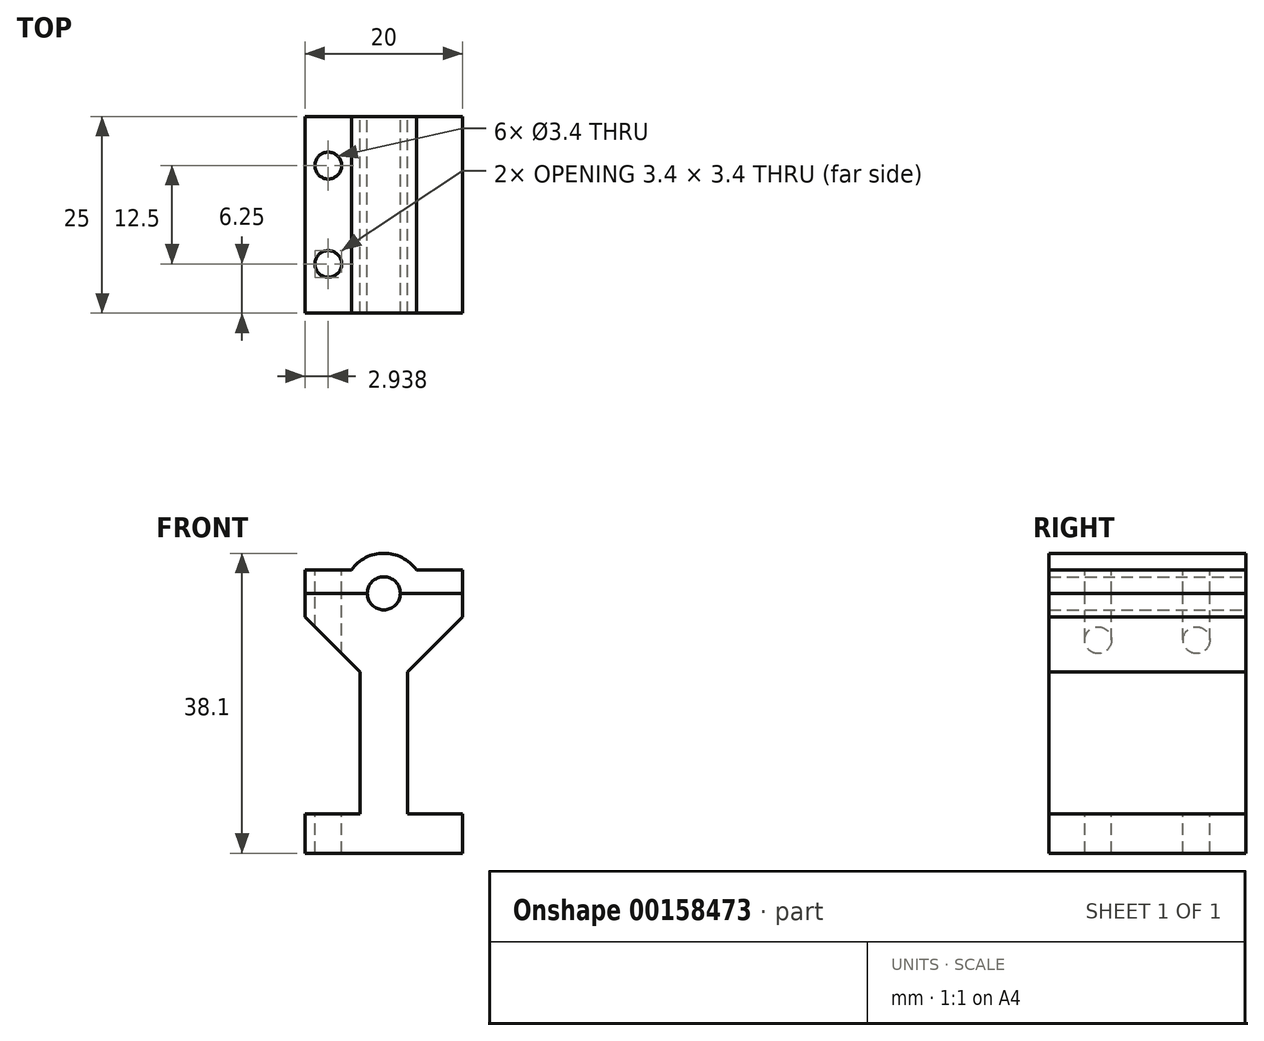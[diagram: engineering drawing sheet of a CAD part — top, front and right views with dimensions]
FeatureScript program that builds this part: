
annotation { "Feature Type Name" : "Feature", "Feature Type Description" : "" }
export const myFeature = defineFeature(function(context is Context, id is Id, definition is map)
    precondition{}
    {
        {
            var Q0;
            Q0=qCreatedBy(makeId("Front.planeOp"),FACE);
            var sketch = newSketch(context, id + "F0", { "sketchPlane" : qUnion([Q0])});
            skLineSegment(sketch, "E0", {"start": v(0, 0) * mm, "end": v(0, 53.37) * mm, "construction": true});
            skLineSegment(sketch, "E1", {"start": v(0, 0) * mm, "end": v(-10, 0) * mm});
            skLineSegment(sketch, "E2", {"start": v(-10, 0) * mm, "end": v(-10, 5) * mm});
            skLineSegment(sketch, "E3", {"start": v(-10, 5) * mm, "end": v(-3, 5) * mm});
            skLineSegment(sketch, "E4", {"start": v(-3, 5) * mm, "end": v(-3, 30) * mm});
            skLineSegment(sketch, "E5", {"start": v(-3, 30) * mm, "end": v(-10, 30) * mm});
            skLineSegment(sketch, "E6", {"start": v(-10, 30) * mm, "end": v(-10, 33) * mm});
            skLineSegment(sketch, "E7", {"start": v(-10, 33) * mm, "end": v(-2.1, 33) * mm});
            skLineSegment(sketch, "E8.MirrorCS", {"start": v(10, 33) * mm, "end": v(2.1, 33) * mm});
            skLineSegment(sketch, "E9.MirrorCS", {"start": v(10, 30) * mm, "end": v(10, 33) * mm});
            skLineSegment(sketch, "E10.MirrorCS", {"start": v(3, 30) * mm, "end": v(10, 30) * mm});
            skLineSegment(sketch, "E11.MirrorCS", {"start": v(3, 5) * mm, "end": v(3, 30) * mm});
            skLineSegment(sketch, "E12.MirrorCS", {"start": v(10, 5) * mm, "end": v(3, 5) * mm});
            skLineSegment(sketch, "E13.MirrorCS", {"start": v(10, 0) * mm, "end": v(10, 5) * mm});
            skLineSegment(sketch, "E14.MirrorCS", {"start": v(0, 0) * mm, "end": v(10, 0) * mm});
            skArc(sketch, "E15", {"start": v(-2.1, 33) * mm, "mid": v(0, 30.9) * mm, "end": v(2.1, 33) * mm});
            skSolve(sketch);
        }
        {
            var Q0;
            Q0=makeQuery(id+"F0.imprint","IMPRINT",FACE,{"disambiguationData":[TD([[makeQuery(id+"F0.imprint","IMPRINT",EDGE,{"derivedFrom":sQuery(id+"F0.wireOp",EDGE,"E1")}),-1.0]])]});
            extrude(context, id + "F1", {"entities" : qUnion([Q0]), "endBound" : BoundingType.SYMMETRIC, "depth" : 25 * mm});
        }
        {
            var Q0;
            Q0=makeQuery(id+"F1.opExtrude","SWEPT_EDGE",EDGE,{"disambiguationData":[OSD([sQuery(id+"F0.wireOp",EDGE,"E4"),sQuery(id+"F0.wireOp",EDGE,"E5")])]});
            var Q1;
            Q1=makeQuery(id+"F1.opExtrude","SWEPT_EDGE",EDGE,{"disambiguationData":[OSD([sQuery(id+"F0.wireOp",EDGE,"E10.MirrorCS"),sQuery(id+"F0.wireOp",EDGE,"E11.MirrorCS")])]});
            chamfer(context, id + "F2", {"entities" : qUnion([Q0, Q1]), "width" : 7 * mm, "tangentPropagation" : true});
        }
        {
            var Q0;
            Q0=qCreatedBy(makeId("Front.planeOp"),FACE);
            var sketch = newSketch(context, id + "F3", { "sketchPlane" : qUnion([Q0])});
            skLineSegment(sketch, "E16", {"start": v(-2.1, 33) * mm, "end": v(-10, 33) * mm});
            skArc(sketch, "E17", {"start": v(2.1, 33) * mm, "mid": v(0, 30.9) * mm, "end": v(-2.1, 33) * mm, "construction": true});
            skLineSegment(sketch, "E18", {"start": v(2.1, 33) * mm, "end": v(10, 33) * mm});
            skArc(sketch, "E19", {"start": v(2.1, 33) * mm, "mid": v(0, 35.1) * mm, "end": v(-2.1, 33) * mm});
            skLineSegment(sketch, "E20.0", {"start": v(-4.12, 36) * mm, "end": v(-10, 36) * mm});
            skArc(sketch, "E20.1", {"start": v(4.12, 36) * mm, "mid": v(0, 38.1) * mm, "end": v(-4.12, 36) * mm});
            skLineSegment(sketch, "E20.2", {"start": v(4.12, 36) * mm, "end": v(10, 36) * mm});
            skLineSegment(sketch, "E21", {"start": v(-10, 33) * mm, "end": v(-10, 36) * mm});
            skLineSegment(sketch, "E22", {"start": v(10, 33) * mm, "end": v(10, 36) * mm});
            skSolve(sketch);
        }
        {
            var Q0;
            Q0=makeQuery(id+"F3.imprint","IMPRINT",FACE,{"disambiguationData":[TD([[makeQuery(id+"F3.imprint","IMPRINT",EDGE,{"derivedFrom":sQuery(id+"F3.wireOp",EDGE,"E16")}),-1.0]])]});
            extrude(context, id + "F4", {"entities" : qUnion([Q0]), "endBound" : BoundingType.SYMMETRIC, "depth" : 25 * mm});
        }
        {
            var Q0;
            Q0=makeQuery(id+"F4.opExtrude","SWEPT_FACE",FACE,{"disambiguationData":[OSD([sQuery(id+"F3.wireOp",EDGE,"E20.0")])]});
            var sketch = newSketch(context, id + "F5", { "sketchPlane" : qUnion([Q0])});
            skLineSegment(sketch, "E23", {"start": v(-7.06, 12.5) * mm, "end": v(-7.06, -12.5) * mm, "construction": true});
            skCircle(sketch, "E24", {"center": v(-7.06, 6.25) * mm, "radius": 1.7 * mm});
            skCircle(sketch, "E25", {"center": v(-7.06, -6.25) * mm, "radius": 1.7 * mm});
            skLineSegment(sketch, "E26", {"start": v(-10, 0) * mm, "end": v(12.13, 0) * mm, "construction": true});
            skPoint(sketch, "E26.endSnap0", {"position": v(-10, 0) * mm});
            skSolve(sketch);
        }
        {
            var Q0;
            Q0 = qSketchRegion(id + "F5", true);
            extrude(context, id + "F6", {"entities" : qUnion([Q0]), "operationType" : NewBodyOperationType.REMOVE, "endBound" : BoundingType.THROUGH_ALL, "oppositeDirection" : true, "depth" : 25 * mm});
        }
        {
            var Q0;
            Q0=makeQuery(id+"F1.opExtrude","SWEPT_FACE",FACE,{"disambiguationData":[OSD([sQuery(id+"F0.wireOp",EDGE,"E7")])]});
            var sketch = newSketch(context, id + "F7", { "sketchPlane" : qUnion([Q0])});
            skCircle(sketch, "E27.0", {"center": v(-7.06, 6.25) * mm, "radius": 1.7 * mm, "construction": true});
            skCircle(sketch, "E28.0", {"center": v(-7.06, -6.25) * mm, "radius": 1.7 * mm, "construction": true});
            skCircle(sketch, "E29", {"center": v(-7.06, 6.25) * mm, "radius": 1.25 * mm});
            skCircle(sketch, "E30", {"center": v(-7.06, -6.25) * mm, "radius": 1.25 * mm});
            skSolve(sketch);
        }
        {
            var Q0;
            Q0 = qSketchRegion(id + "F7", true);
            extrude(context, id + "F8", {"entities" : qUnion([Q0]), "operationType" : NewBodyOperationType.REMOVE, "endBound" : BoundingType.THROUGH_ALL, "oppositeDirection" : true, "depth" : 25 * mm});
        }
    });
